# Revit family: Калитка_PROM_H1300-2500
name_source: partatom
category: Специальное оборудование
units: mm (PartAtom-declared; Revit-internal decimal feet)

## family parameters
Всегда вертикально = Да
На основе рабочей плоскости = Нет
Общий = Нет
При загрузке вырезать с полостями = Нет
Размер круглого соединителя = Использовать диаметр
Тип детали = Нормальный
Точка расчета площади = Нет

## types (8) — shared parameters
ADSK_Единица измерения = шт.
ADSK_Завод-изготовитель = FENSYS
ADSK_Комплект = Калитка
URL = https://www.fensys.ru
Изготовитель = FENSYS
Материал_Сетка = FENSYS_Сетка_50x100
Материал_Столбы = FENSYS_Столб
Ширина рамки = 60 мм

## per-type parameters (varying)
| type | ADSK_Обозначение | PROM 2 P2F | PROM PF | PROM_Н | Бетонирование в кондукторе | Бетонирование столбы (SI) | Высота Замка | Глубина столба | Тип креплния | Фланец | Фланец под винтовую опору |
| PROM PF_Фланец под винтовую опору | PROM/SITgs | Нет | Да | PROM | Нет | Нет | 1040 мм | 0 мм | 4 | Нет | Да |
| PROM PF_Фланец | PROM/SIT | Нет | Да | PROM | Нет | Нет | 1040 мм | 0 мм | 3 | Да | Нет |
| PROM2 P2F_Фланец | PROM2 /SIT | Да | Нет | PROM2 | Нет | Нет | 1040 мм | 0 мм | 3 | Да | Нет |
| PROM2 P2F_Фланец под винтовую опору | PROM2 /SITgs | Да | Нет | PROM2 | Нет | Нет | 1040 мм | 0 мм | 4 | Нет | Да |
| PROM2 P2F_Бетонирование в кондукторе | PROM2 /SIC | Да | Нет | PROM2 | Да | Нет | 1040 мм | 500 мм | 1 | Нет | Нет |
| PROM PF_Бетонирование в кондукторе | PROM/SIC | Нет | Да | PROM | Да | Нет | 1050 мм | 500 мм | 1 | Нет | Нет |
| PROM PF_Бетонирование столбы (SI) | PROM/SI | Нет | Да | PROM | Нет | Да | 1040 мм | 500 мм | 2 | Нет | Нет |
| PROM2 P2F_Бетонирование столбы (SI) | PROM2 /SI | Да | Нет | PROM2 | Нет | Да | 1040 мм | 500 мм | 2 | Нет | Нет |
